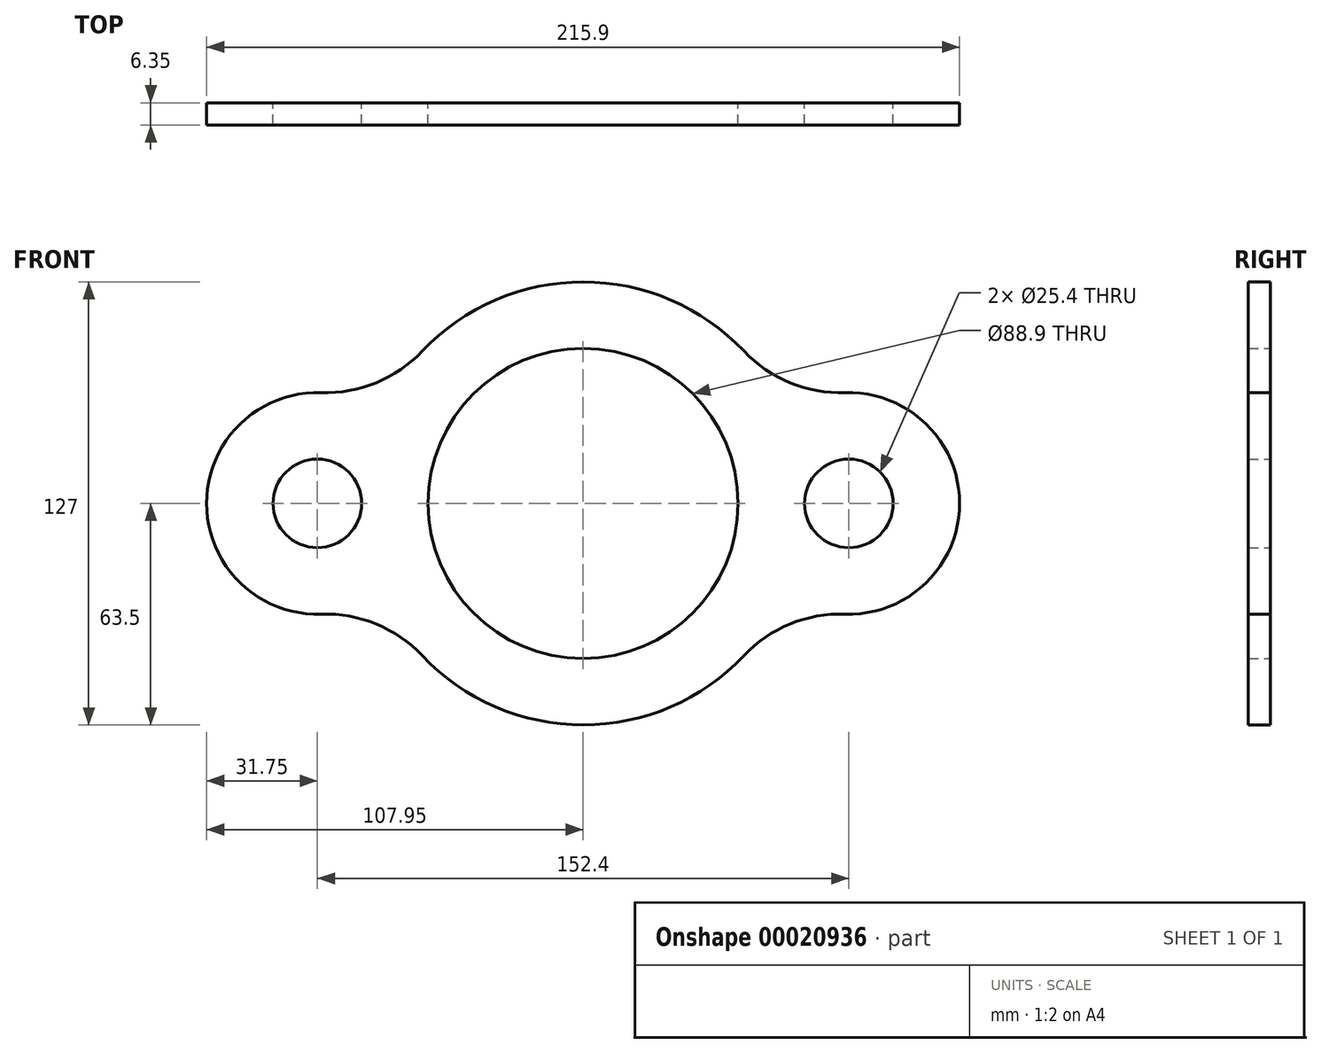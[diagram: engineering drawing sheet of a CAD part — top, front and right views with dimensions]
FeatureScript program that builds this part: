
annotation { "Feature Type Name" : "Feature", "Feature Type Description" : "" }
export const myFeature = defineFeature(function(context is Context, id is Id, definition is map)
    precondition{}
    {
        {
            var Q0;
            Q0=qCreatedBy(makeId("Front.planeOp"),FACE);
            var sketch = newSketch(context, id + "F0", { "sketchPlane" : qUnion([Q0])});
            skCircle(sketch, "E0", {"center": v(0, 0) * mm, "radius": 44.45 * mm});
            skArc(sketch, "E1", {"start": v(-46.14, -43.63) * mm, "mid": v(0, -63.5) * mm, "end": v(46.14, -43.63) * mm});
            skLineSegment(sketch, "E2", {"start": v(-85, 0) * mm, "end": v(105.3, 0) * mm, "construction": true});
            skCircle(sketch, "E3", {"center": v(-76.2, 0) * mm, "radius": 12.7 * mm});
            skArc(sketch, "E4", {"start": v(-75.12, 31.73) * mm, "mid": v(-107.95, 0) * mm, "end": v(-75.12, -31.73) * mm});
            skCircle(sketch, "E5", {"center": v(76.2, 0) * mm, "radius": 12.7 * mm});
            skArc(sketch, "E6", {"start": v(75.12, -31.73) * mm, "mid": v(107.95, 0) * mm, "end": v(75.12, 31.73) * mm});
            skArc(sketch, "E7.trimOffspring", {"start": v(46.14, 43.63) * mm, "mid": v(0, 63.5) * mm, "end": v(-46.14, 43.63) * mm});
            skPoint(sketch, "E8.visualSharp", {"position": v(-57.94, 25.98) * mm});
            skArc(sketch, "E8.filletArc", {"start": v(-75.12, 31.73) * mm, "mid": v(-59.35, 34.56) * mm, "end": v(-46.14, 43.63) * mm});
            skPoint(sketch, "E9.visualSharp", {"position": v(57.94, 25.98) * mm});
            skArc(sketch, "E9.filletArc", {"start": v(46.14, 43.63) * mm, "mid": v(59.35, 34.56) * mm, "end": v(75.12, 31.73) * mm});
            skPoint(sketch, "E10.visualSharp", {"position": v(57.94, -25.98) * mm});
            skArc(sketch, "E10.filletArc", {"start": v(75.12, -31.73) * mm, "mid": v(59.35, -34.56) * mm, "end": v(46.14, -43.63) * mm});
            skPoint(sketch, "E11.visualSharp", {"position": v(-57.94, -25.98) * mm});
            skArc(sketch, "E11.filletArc", {"start": v(-46.14, -43.63) * mm, "mid": v(-59.35, -34.56) * mm, "end": v(-75.12, -31.73) * mm});
            skSolve(sketch);
        }
        {
            var Q0;
            Q0=makeQuery(id+"F0.imprint","IMPRINT",FACE,{"disambiguationData":[TD([[makeQuery(id+"F0.imprint","IMPRINT",EDGE,{"derivedFrom":sQuery(id+"F0.wireOp",EDGE,"E0")}),-1.0]])]});
            extrude(context, id + "F1", {"entities" : qUnion([Q0]), "depth" : 6.35 * mm});
        }
    });
